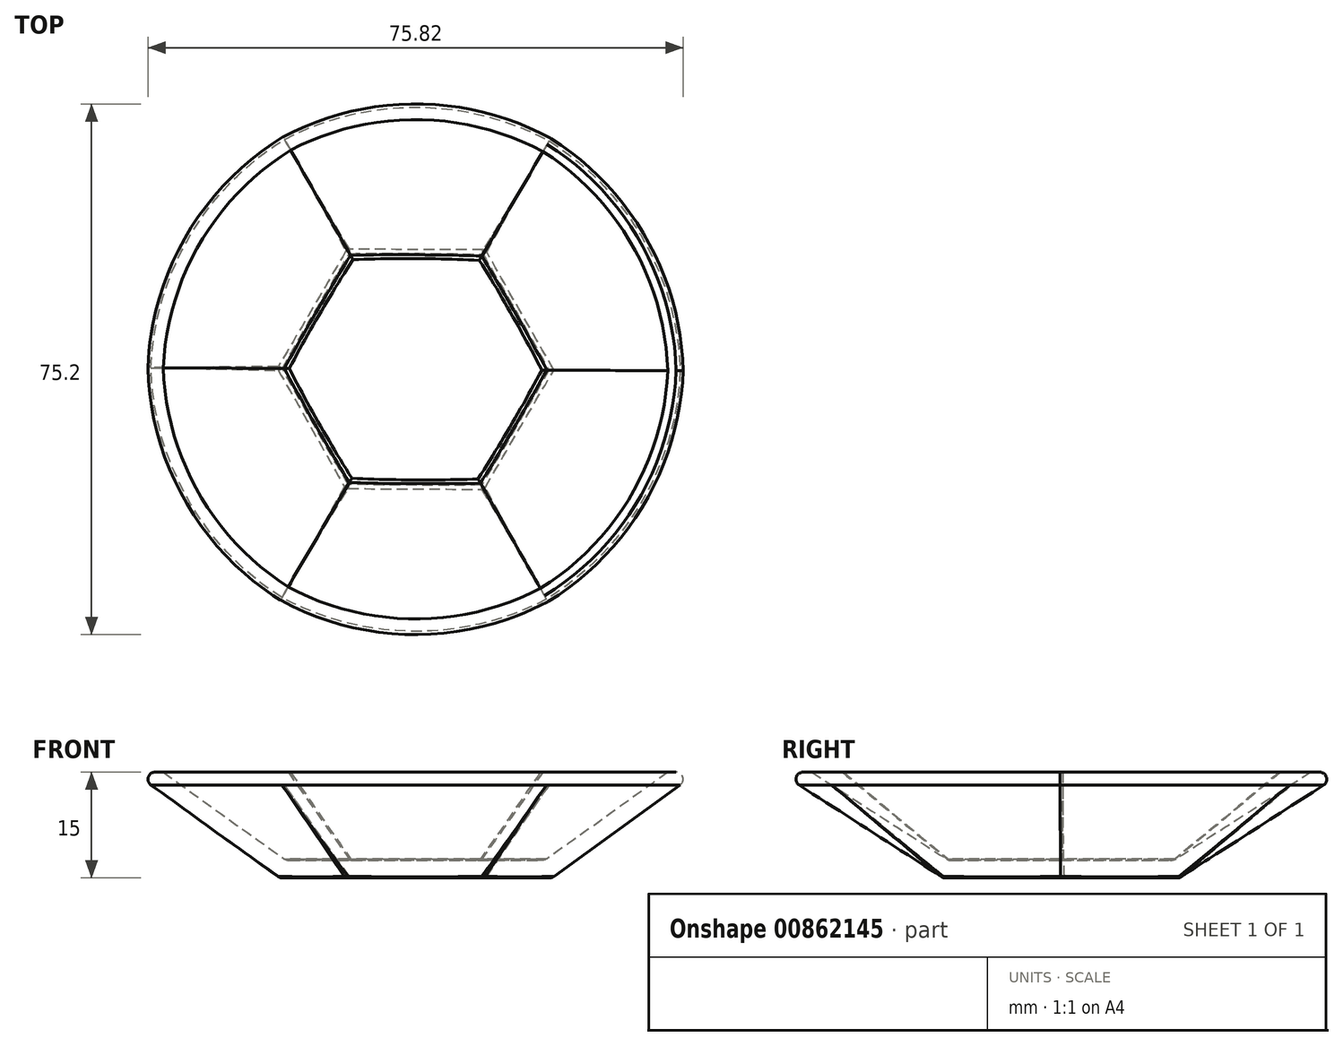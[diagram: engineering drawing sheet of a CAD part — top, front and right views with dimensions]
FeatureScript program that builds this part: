
annotation { "Feature Type Name" : "Feature", "Feature Type Description" : "" }
export const myFeature = defineFeature(function(context is Context, id is Id, definition is map)
    precondition{}
    {
        {
            var Q0;
            Q0=qCreatedBy(makeId("Top.planeOp"),FACE);
            var sketch = newSketch(context, id + "F0", { "sketchPlane" : qUnion([Q0])});
            skCircle(sketch, "E0", {"center": v(0, 0) * mm, "radius": 40 * mm});
            skSolve(sketch);
        }
        {
            var Q0;
            Q0=qCreatedBy(makeId("Top.planeOp"),FACE);
            cPlane(context, id + "F1", {"entities" : qUnion([Q0]), "cplaneType" : CPlaneType.OFFSET, "offset" : 15 * mm, "oppositeDirection" : true, "width" : 150 * mm, "height" : 150 * mm});
        }
        {
            var Q0;
            Q0=qCreatedBy(id+"F1.planeOp",FACE);
            var sketch = newSketch(context, id + "F2", { "sketchPlane" : qUnion([Q0])});
            skCircle(sketch, "E1.cCircle", {"center": v(0, 0) * mm, "radius": 16.7 * mm, "construction": true});
            skLineSegment(sketch, "E1.0", {"start": v(9.74, 16.65) * mm, "end": v(19.3, -0.11) * mm});
            skLineSegment(sketch, "E1.1", {"start": v(19.3, -0.11) * mm, "end": v(9.55, -16.77) * mm});
            skLineSegment(sketch, "E1.2", {"start": v(9.55, -16.77) * mm, "end": v(-9.74, -16.65) * mm});
            skLineSegment(sketch, "E1.3", {"start": v(-9.74, -16.65) * mm, "end": v(-19.3, 0.11) * mm});
            skLineSegment(sketch, "E1.4", {"start": v(-19.3, 0.11) * mm, "end": v(-9.55, 16.77) * mm});
            skLineSegment(sketch, "E1.5", {"start": v(-9.55, 16.77) * mm, "end": v(9.74, 16.65) * mm});
            skPoint(sketch, "E1.0.midPoint", {"position": v(14.52, 8.27) * mm});
            skSolve(sketch);
        }
        {
            var Q0;
            Q0=makeQuery(id+"F0.imprint","IMPRINT",FACE,{"disambiguationData":[TD([[makeQuery(id+"F0.imprint","IMPRINT",EDGE,{"derivedFrom":sQuery(id+"F0.wireOp",EDGE,"E0")}),1.0]])]});
            var Q1;
            Q1=makeQuery(id+"F2.imprint","IMPRINT",FACE,{"disambiguationData":[TD([[makeQuery(id+"F2.imprint","IMPRINT",EDGE,{"derivedFrom":sQuery(id+"F2.wireOp",EDGE,"E1.0")}),-1.0]])]});
            loft(context, id + "F3", {"sheetProfilesArray" : [{ "sheetProfileEntities" : qUnion([Q0]) }, { "sheetProfileEntities" : qUnion([Q1]) }]});
        }
        {
            var Q0;
            Q0=makeQuery(id+"F3.opLoft","CAP_FACE",FACE,{"disambiguationData":[OSD([makeQuery(id+"F0.imprint","IMPRINT",FACE,{"disambiguationData":[TD([[makeQuery(id+"F0.imprint","IMPRINT",EDGE,{"derivedFrom":sQuery(id+"F0.wireOp",EDGE,"E0")}),1.0]])]})])],"isStart":true});
            shell(context, id + "F4", {"entities" : qUnion([Q0]), "thickness" : 2.5 * mm});
        }
        {
            var Q0;
            Q0=makeQuery(id+"F3.opLoft","MID_CAP_EDGE",EDGE,{"disambiguationData":[OSD([sQuery(id+"F0.wireOp",EDGE,"E0"),sQuery(id+"F2.wireOp",EDGE,"E1.0"),sQuery(id+"F2.wireOp",EDGE,"E1.1"),sQuery(id+"F2.wireOp",EDGE,"E1.5")])],"capPos":0.0});
            var Q1;
            Q1=makeQuery(id+"F3.opLoft","MID_CAP_EDGE",EDGE,{"disambiguationData":[OSD([sQuery(id+"F0.wireOp",EDGE,"E0"),sQuery(id+"F2.wireOp",EDGE,"E1.0"),sQuery(id+"F2.wireOp",EDGE,"E1.5")])],"capPos":0.0});
            var Q2;
            Q2=makeQuery(id+"F3.opLoft","MID_CAP_EDGE",EDGE,{"disambiguationData":[OSD([sQuery(id+"F0.wireOp",EDGE,"E0"),sQuery(id+"F2.wireOp",EDGE,"E1.0"),sQuery(id+"F2.wireOp",EDGE,"E1.3"),sQuery(id+"F2.wireOp",EDGE,"E1.4"),sQuery(id+"F2.wireOp",EDGE,"E1.5")])],"capPos":0.0});
            var Q3;
            Q3=makeQuery(id+"F3.opLoft","MID_CAP_EDGE",EDGE,{"disambiguationData":[OSD([sQuery(id+"F0.wireOp",EDGE,"E0"),sQuery(id+"F2.wireOp",EDGE,"E1.1"),sQuery(id+"F2.wireOp",EDGE,"E1.2"),sQuery(id+"F2.wireOp",EDGE,"E1.3")])],"capPos":0.0});
            var Q4;
            Q4=makeQuery(id+"F3.opLoft","MID_CAP_EDGE",EDGE,{"disambiguationData":[OSD([sQuery(id+"F0.wireOp",EDGE,"E0"),sQuery(id+"F2.wireOp",EDGE,"E1.0"),sQuery(id+"F2.wireOp",EDGE,"E1.1"),sQuery(id+"F2.wireOp",EDGE,"E1.2")])],"capPos":0.0});
            var Q5;
            Q5=makeQuery(id+"F3.opLoft","MID_CAP_EDGE",EDGE,{"disambiguationData":[OSD([sQuery(id+"F0.wireOp",EDGE,"E0"),sQuery(id+"F2.wireOp",EDGE,"E1.2"),sQuery(id+"F2.wireOp",EDGE,"E1.3"),sQuery(id+"F2.wireOp",EDGE,"E1.4")])],"capPos":0.0});
            fillet(context, id + "F5", {"entities" : qUnion([Q0, Q1, Q2, Q3, Q4, Q5]), "radius" : 1 * mm, "tangentPropagation" : true, "allowEdgeOverflow" : false});
        }
        {
            var Q0;
            Q0=makeQuery(id+"F3.opLoft","MID_CAP_EDGE",EDGE,{"disambiguationData":[OSD([sQuery(id+"F2.wireOp",EDGE,"E1.0"),sQuery(id+"F2.wireOp",EDGE,"E1.1"),sQuery(id+"F2.wireOp",EDGE,"E1.2")])],"capPos":1.0});
            var Q1;
            Q1=makeQuery(id+"F3.opLoft","MID_CAP_EDGE",EDGE,{"disambiguationData":[OSD([sQuery(id+"F2.wireOp",EDGE,"E1.0"),sQuery(id+"F2.wireOp",EDGE,"E1.1"),sQuery(id+"F2.wireOp",EDGE,"E1.5")])],"capPos":1.0});
            var Q2;
            Q2=makeQuery(id+"F3.opLoft","MID_CAP_EDGE",EDGE,{"disambiguationData":[OSD([sQuery(id+"F2.wireOp",EDGE,"E1.0"),sQuery(id+"F2.wireOp",EDGE,"E1.4"),sQuery(id+"F2.wireOp",EDGE,"E1.5")])],"capPos":1.0});
            var Q3;
            Q3=makeQuery(id+"F3.opLoft","MID_CAP_EDGE",EDGE,{"disambiguationData":[OSD([sQuery(id+"F2.wireOp",EDGE,"E1.3"),sQuery(id+"F2.wireOp",EDGE,"E1.4"),sQuery(id+"F2.wireOp",EDGE,"E1.5")])],"capPos":1.0});
            var Q4;
            Q4=makeQuery(id+"F3.opLoft","MID_CAP_EDGE",EDGE,{"disambiguationData":[OSD([sQuery(id+"F2.wireOp",EDGE,"E1.2"),sQuery(id+"F2.wireOp",EDGE,"E1.3"),sQuery(id+"F2.wireOp",EDGE,"E1.4")])],"capPos":1.0});
            var Q5;
            Q5=makeQuery(id+"F3.opLoft","MID_CAP_EDGE",EDGE,{"disambiguationData":[OSD([sQuery(id+"F2.wireOp",EDGE,"E1.1"),sQuery(id+"F2.wireOp",EDGE,"E1.2"),sQuery(id+"F2.wireOp",EDGE,"E1.3")])],"capPos":1.0});
            fillet(context, id + "F6", {"entities" : qUnion([Q0, Q1, Q2, Q3, Q4, Q5]), "radius" : 1 * mm, "tangentPropagation" : true, "allowEdgeOverflow" : false});
        }
        {
            var Q0;
            Q0=makeQuery(id+"F3.opLoft","SWEPT_EDGE",EDGE,{"disambiguationData":[OSD([sQuery(id+"F0.wireOp",EDGE,"E0"),sQuery(id+"F2.wireOp",EDGE,"E1.0"),sQuery(id+"F2.wireOp",EDGE,"E1.1"),sQuery(id+"F2.wireOp",EDGE,"E1.5")])]});
            var Q1;
            Q1=makeQuery(id+"F3.opLoft","SWEPT_EDGE",EDGE,{"disambiguationData":[OSD([sQuery(id+"F2.wireOp",EDGE,"E1.0"),sQuery(id+"F2.wireOp",EDGE,"E1.5")])]});
            var Q2;
            Q2=makeQuery(id+"F3.opLoft","SWEPT_EDGE",EDGE,{"disambiguationData":[OSD([sQuery(id+"F0.wireOp",EDGE,"E0"),sQuery(id+"F2.wireOp",EDGE,"E1.3"),sQuery(id+"F2.wireOp",EDGE,"E1.4"),sQuery(id+"F2.wireOp",EDGE,"E1.5")])]});
            var Q3;
            Q3=makeQuery(id+"F3.opLoft","SWEPT_EDGE",EDGE,{"disambiguationData":[OSD([sQuery(id+"F0.wireOp",EDGE,"E0"),sQuery(id+"F2.wireOp",EDGE,"E1.2"),sQuery(id+"F2.wireOp",EDGE,"E1.3"),sQuery(id+"F2.wireOp",EDGE,"E1.4")])]});
            var Q4;
            Q4=makeQuery(id+"F3.opLoft","SWEPT_EDGE",EDGE,{"disambiguationData":[OSD([sQuery(id+"F0.wireOp",EDGE,"E0"),sQuery(id+"F2.wireOp",EDGE,"E1.1"),sQuery(id+"F2.wireOp",EDGE,"E1.2"),sQuery(id+"F2.wireOp",EDGE,"E1.3")])]});
            var Q5;
            Q5=makeQuery(id+"F3.opLoft","SWEPT_EDGE",EDGE,{"disambiguationData":[OSD([sQuery(id+"F0.wireOp",EDGE,"E0"),sQuery(id+"F2.wireOp",EDGE,"E1.0"),sQuery(id+"F2.wireOp",EDGE,"E1.1"),sQuery(id+"F2.wireOp",EDGE,"E1.2")])]});
            fillet(context, id + "F7", {"entities" : qUnion([Q0, Q1, Q2, Q3, Q4, Q5]), "radius" : 1 * mm, "tangentPropagation" : true, "allowEdgeOverflow" : false});
        }
        {
            var Q0;
            Q0=makeQuery(id+"F4.opShell","OFFSET_EDGE",EDGE,{"disambiguationData":[OSD([sQuery(id+"F2.wireOp",EDGE,"E1.3"),sQuery(id+"F2.wireOp",EDGE,"E1.4"),sQuery(id+"F2.wireOp",EDGE,"E1.5")])]});
            var Q1;
            Q1=makeQuery(id+"F4.opShell","OFFSET_EDGE",EDGE,{"disambiguationData":[OSD([sQuery(id+"F2.wireOp",EDGE,"E1.0"),sQuery(id+"F2.wireOp",EDGE,"E1.4"),sQuery(id+"F2.wireOp",EDGE,"E1.5")])]});
            var Q2;
            Q2=makeQuery(id+"F4.opShell","OFFSET_EDGE",EDGE,{"disambiguationData":[OSD([sQuery(id+"F2.wireOp",EDGE,"E1.0"),sQuery(id+"F2.wireOp",EDGE,"E1.1"),sQuery(id+"F2.wireOp",EDGE,"E1.5")])]});
            var Q3;
            Q3=makeQuery(id+"F4.opShell","OFFSET_EDGE",EDGE,{"disambiguationData":[OSD([sQuery(id+"F2.wireOp",EDGE,"E1.2"),sQuery(id+"F2.wireOp",EDGE,"E1.3"),sQuery(id+"F2.wireOp",EDGE,"E1.4")])]});
            var Q4;
            Q4=makeQuery(id+"F4.opShell","OFFSET_EDGE",EDGE,{"disambiguationData":[OSD([sQuery(id+"F2.wireOp",EDGE,"E1.1"),sQuery(id+"F2.wireOp",EDGE,"E1.2"),sQuery(id+"F2.wireOp",EDGE,"E1.3")])]});
            var Q5;
            Q5=makeQuery(id+"F4.opShell","OFFSET_EDGE",EDGE,{"disambiguationData":[OSD([sQuery(id+"F2.wireOp",EDGE,"E1.0"),sQuery(id+"F2.wireOp",EDGE,"E1.1"),sQuery(id+"F2.wireOp",EDGE,"E1.2")])]});
            fillet(context, id + "F8", {"entities" : qUnion([Q0, Q1, Q2, Q3, Q4, Q5]), "radius" : 1 * mm, "tangentPropagation" : true, "allowEdgeOverflow" : false});
        }
    });
